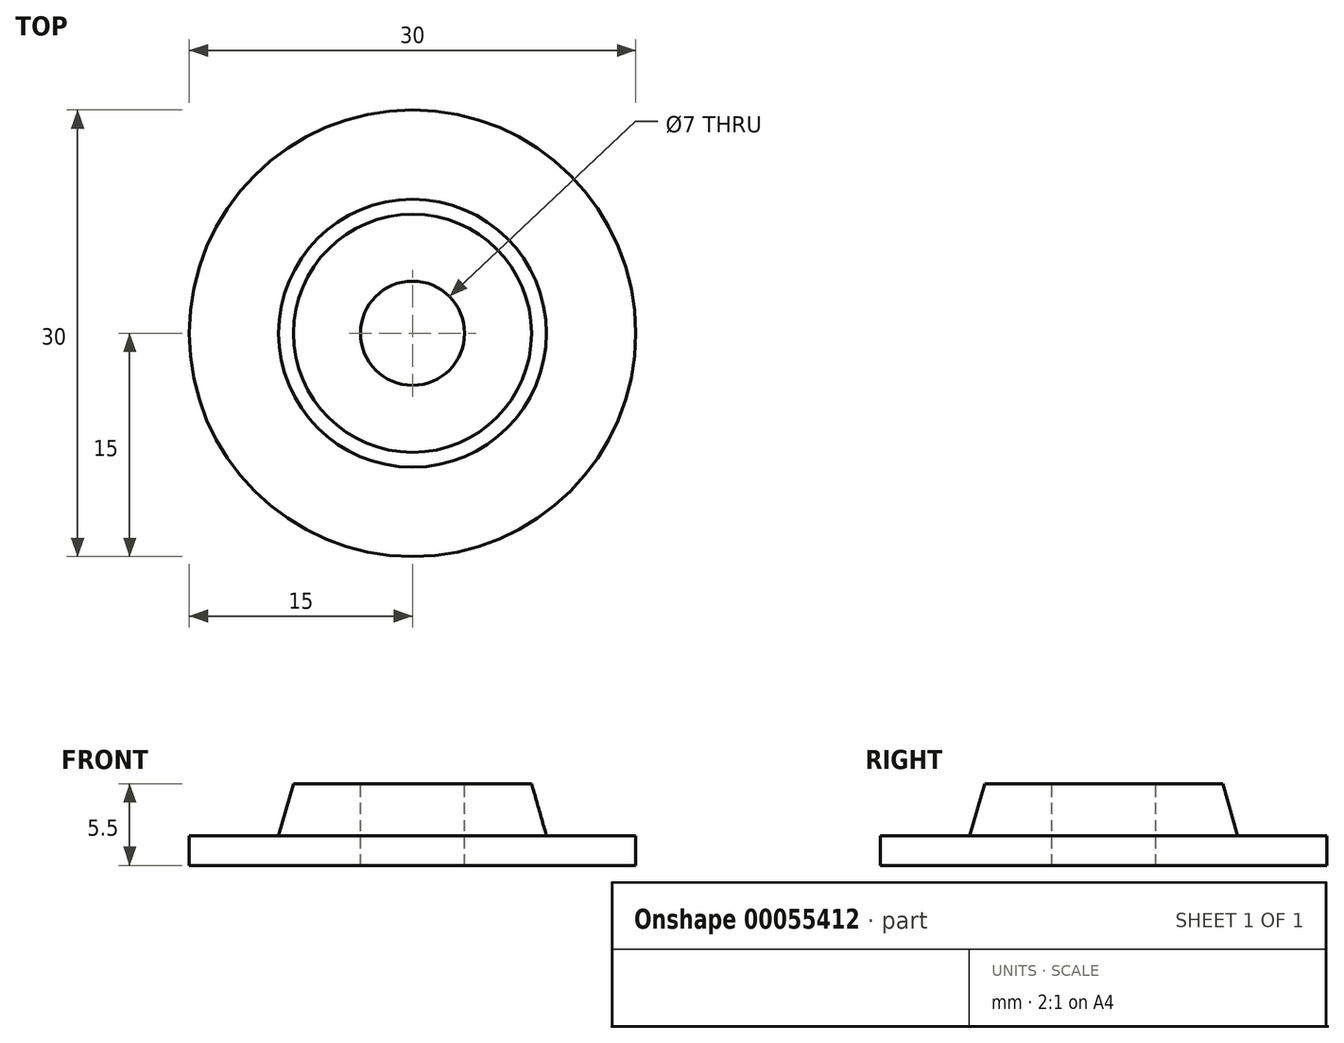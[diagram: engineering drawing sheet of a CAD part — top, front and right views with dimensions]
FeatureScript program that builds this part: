
annotation { "Feature Type Name" : "Feature", "Feature Type Description" : "" }
export const myFeature = defineFeature(function(context is Context, id is Id, definition is map)
    precondition{}
    {
        {
            var Q0;
            Q0=qCreatedBy(makeId("Front.planeOp"),FACE);
            var sketch = newSketch(context, id + "F0", { "sketchPlane" : qUnion([Q0])});
            skLineSegment(sketch, "E0", {"start": v(-15, 0) * mm, "end": v(-15, 2) * mm});
            skLineSegment(sketch, "E1", {"start": v(-15, 2) * mm, "end": v(-9, 2) * mm});
            skLineSegment(sketch, "E2", {"start": v(-9, 2) * mm, "end": v(-8, 5.5) * mm});
            skLineSegment(sketch, "E3", {"start": v(-8, 5.5) * mm, "end": v(-3.5, 5.5) * mm});
            skLineSegment(sketch, "E4", {"start": v(-3.5, 5.5) * mm, "end": v(-3.5, 0) * mm});
            skLineSegment(sketch, "E5", {"start": v(-3.5, 0) * mm, "end": v(-15, 0) * mm});
            skLineSegment(sketch, "E6", {"start": v(0, 42.7) * mm, "end": v(0, -32.05) * mm, "construction": true});
            skSolve(sketch);
        }
        {
            var Q0;
            Q0=makeQuery(id+"F0.imprint","IMPRINT",FACE,{"disambiguationData":[TD([[makeQuery(id+"F0.imprint","IMPRINT",EDGE,{"derivedFrom":sQuery(id+"F0.wireOp",EDGE,"E0")}),-1.0]])]});
            var Q1;
            Q1=sQuery(id+"F0.wireOp",EDGE,"E6");
            revolve(context, id + "F1", {"entities" : qUnion([Q0]), "axis" : qUnion([Q1]), "revolveType" : RevolveType.FULL});
        }
    });
